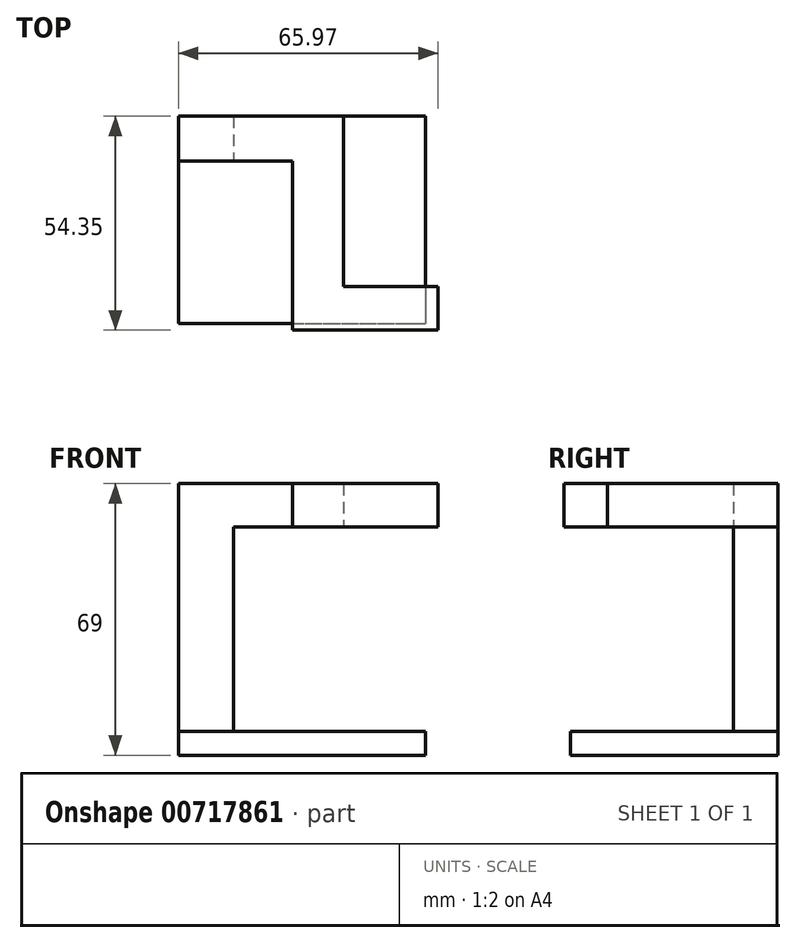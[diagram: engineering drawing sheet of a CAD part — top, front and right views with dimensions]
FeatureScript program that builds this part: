
annotation { "Feature Type Name" : "Feature", "Feature Type Description" : "" }
export const myFeature = defineFeature(function(context is Context, id is Id, definition is map)
    precondition{}
    {
        {
            var Q0;
            Q0=qCreatedBy(makeId("Top.planeOp"),FACE);
            var sketch = newSketch(context, id + "F0", { "sketchPlane" : qUnion([Q0])});
            skLineSegment(sketch, "E0.bottom", {"start": v(-28.96, 22.77) * mm, "end": v(33.89, 22.77) * mm});
            skLineSegment(sketch, "E0.top", {"start": v(-28.96, -29.91) * mm, "end": v(33.89, -29.91) * mm});
            skLineSegment(sketch, "E0.left", {"start": v(-28.96, 22.77) * mm, "end": v(-28.96, -29.91) * mm});
            skLineSegment(sketch, "E0.right", {"start": v(33.89, 22.77) * mm, "end": v(33.89, -29.91) * mm});
            skSolve(sketch);
        }
        {
            var Q0;
            Q0 = qSketchRegion(id + "F0", true);
            extrude(context, id + "F1", {"entities" : qUnion([Q0]), "depth" : 6 * mm, "offsetDistance" : 25 * mm});
        }
        {
            var Q0;
            Q0=makeQuery(id+"F1.opExtrude","CAP_FACE",FACE,{"disambiguationData":[OSD([sQuery(id+"F0.wireOp",EDGE,"E0.bottom"),sQuery(id+"F0.wireOp",EDGE,"E0.top"),sQuery(id+"F0.wireOp",EDGE,"E0.left"),sQuery(id+"F0.wireOp",EDGE,"E0.right")])],"isStart":false});
            var sketch = newSketch(context, id + "F2", { "sketchPlane" : qUnion([Q0])});
            skLineSegment(sketch, "E1.bottom", {"start": v(-28.96, 22.77) * mm, "end": v(-15, 22.77) * mm});
            skLineSegment(sketch, "E1.top", {"start": v(-28.96, 11.42) * mm, "end": v(-15, 11.42) * mm});
            skLineSegment(sketch, "E1.left", {"start": v(-28.96, 22.77) * mm, "end": v(-28.96, 11.42) * mm});
            skLineSegment(sketch, "E1.right", {"start": v(-15, 22.77) * mm, "end": v(-15, 11.42) * mm});
            skSolve(sketch);
        }
        {
            var Q0;
            Q0 = qSketchRegion(id + "F2", true);
            extrude(context, id + "F3", {"entities" : qUnion([Q0]), "operationType" : NewBodyOperationType.ADD, "depth" : 63 * mm, "offsetDistance" : 25 * mm});
        }
        {
            var Q0;
            Q0=makeQuery(id+"F3.opExtrude","SWEPT_FACE",FACE,{"disambiguationData":[OSD([sQuery(id+"F2.wireOp",EDGE,"E1.right")])]});
            var sketch = newSketch(context, id + "F4", { "sketchPlane" : qUnion([Q0])});
            skLineSegment(sketch, "E2.bottom", {"start": v(11.42, 69) * mm, "end": v(22.77, 69) * mm});
            skLineSegment(sketch, "E2.top", {"start": v(11.42, 57.96) * mm, "end": v(22.77, 57.96) * mm});
            skLineSegment(sketch, "E2.left", {"start": v(11.42, 69) * mm, "end": v(11.42, 57.96) * mm});
            skLineSegment(sketch, "E2.right", {"start": v(22.77, 69) * mm, "end": v(22.77, 57.96) * mm});
            skSolve(sketch);
        }
        {
            var Q0;
            Q0 = qSketchRegion(id + "F4", true);
            extrude(context, id + "F5", {"entities" : qUnion([Q0]), "operationType" : NewBodyOperationType.ADD, "depth" : 28 * mm, "offsetDistance" : 25 * mm});
        }
        {
            var Q0;
            Q0=makeQuery(id+"F5.boolean.opBoolean","MERGE",FACE,{"derivedFrom":[makeQuery(id+"F3.opExtrude","SWEPT_FACE",FACE,{"disambiguationData":[OSD([sQuery(id+"F2.wireOp",EDGE,"E1.top")])]}),makeQuery(id+"F5.opExtrude","SWEPT_FACE",FACE,{"disambiguationData":[OSD([sQuery(id+"F4.wireOp",EDGE,"E2.left")])]})]});
            var sketch = newSketch(context, id + "F6", { "sketchPlane" : qUnion([Q0])});
            skLineSegment(sketch, "E3.bottom", {"start": v(13, 69) * mm, "end": v(0, 69) * mm});
            skLineSegment(sketch, "E3.top", {"start": v(13, 57.96) * mm, "end": v(0, 57.96) * mm});
            skLineSegment(sketch, "E3.left", {"start": v(13, 69) * mm, "end": v(13, 57.96) * mm});
            skLineSegment(sketch, "E3.right", {"start": v(0, 69) * mm, "end": v(0, 57.96) * mm});
            skSolve(sketch);
        }
        {
            var Q0;
            Q0 = qSketchRegion(id + "F6", true);
            extrude(context, id + "F7", {"entities" : qUnion([Q0]), "operationType" : NewBodyOperationType.ADD, "depth" : 43 * mm, "offsetDistance" : 25 * mm});
        }
        {
            var Q0;
            Q0=makeQuery(id+"F7.boolean.opBoolean","MERGE",FACE,{"derivedFrom":[makeQuery(id+"F5.opExtrude","CAP_FACE",FACE,{"disambiguationData":[OSD([sQuery(id+"F4.wireOp",EDGE,"E2.bottom"),sQuery(id+"F4.wireOp",EDGE,"E2.top"),sQuery(id+"F4.wireOp",EDGE,"E2.left"),sQuery(id+"F4.wireOp",EDGE,"E2.right")])],"isStart":false}),makeQuery(id+"F7.opExtrude","SWEPT_FACE",FACE,{"disambiguationData":[OSD([sQuery(id+"F6.wireOp",EDGE,"E3.left")])]})]});
            var sketch = newSketch(context, id + "F8", { "sketchPlane" : qUnion([Q0])});
            skLineSegment(sketch, "E4.bottom", {"start": v(-31.58, 69) * mm, "end": v(-20.47, 69) * mm});
            skLineSegment(sketch, "E4.top", {"start": v(-31.58, 57.96) * mm, "end": v(-20.47, 57.96) * mm});
            skLineSegment(sketch, "E4.left", {"start": v(-31.58, 69) * mm, "end": v(-31.58, 57.96) * mm});
            skLineSegment(sketch, "E4.right", {"start": v(-20.47, 69) * mm, "end": v(-20.47, 57.96) * mm});
            skSolve(sketch);
        }
        {
            var Q0;
            Q0 = qSketchRegion(id + "F8", true);
            extrude(context, id + "F9", {"entities" : qUnion([Q0]), "operationType" : NewBodyOperationType.ADD, "depth" : 24 * mm, "offsetDistance" : 25 * mm});
        }
    });
